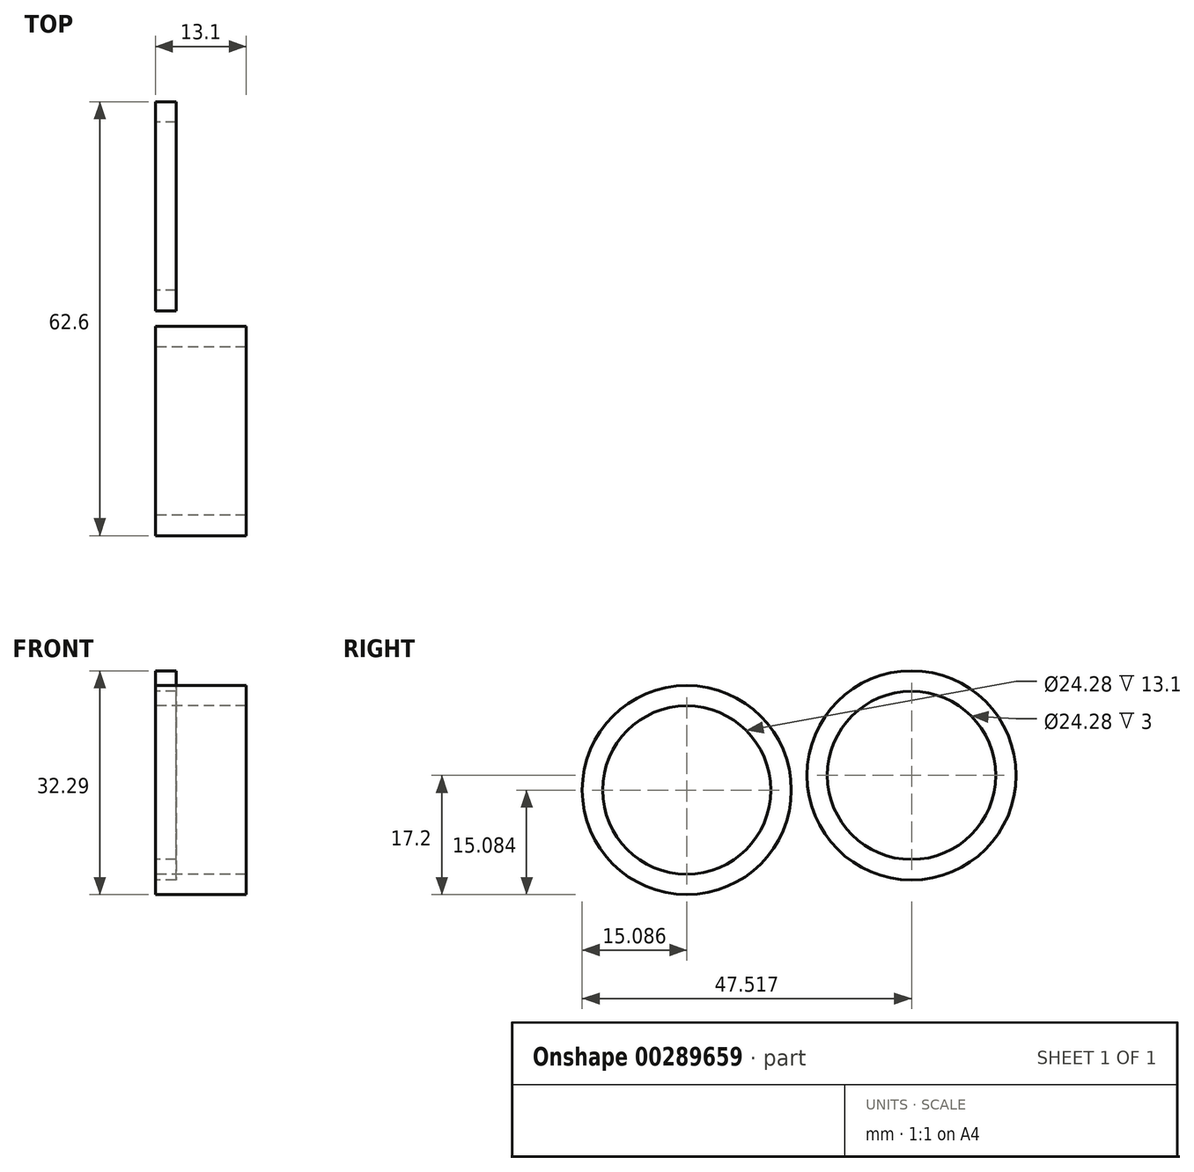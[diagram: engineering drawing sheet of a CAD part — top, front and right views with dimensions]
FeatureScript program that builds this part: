
annotation { "Feature Type Name" : "Feature", "Feature Type Description" : "" }
export const myFeature = defineFeature(function(context is Context, id is Id, definition is map)
    precondition{}
    {
        {
            var Q0;
            Q0=qCreatedBy(makeId("Right.planeOp"),FACE);
            var sketch = newSketch(context, id + "F0", { "sketchPlane" : qUnion([Q0])});
            skCircle(sketch, "E0", {"center": v(-30.12, 34.57) * mm, "radius": 15.09 * mm});
            skCircle(sketch, "E1", {"center": v(-30.12, 34.57) * mm, "radius": 12.14 * mm});
            skSolve(sketch);
        }
        {
            var Q0;
            Q0=makeQuery(id+"F0.imprint","IMPRINT",FACE,{"disambiguationData":[TD([[makeQuery(id+"F0.imprint","IMPRINT",EDGE,{"derivedFrom":sQuery(id+"F0.wireOp",EDGE,"E0")}),1.0]])]});
            extrude(context, id + "F1", {"entities" : qUnion([Q0]), "depth" : 3 * mm});
        }
        {
            var Q0;
            Q0=qCreatedBy(makeId("Right.planeOp"),FACE);
            var sketch = newSketch(context, id + "F2", { "sketchPlane" : qUnion([Q0])});
            skCircle(sketch, "E2", {"center": v(-62.55, 32.45) * mm, "radius": 15.09 * mm});
            skCircle(sketch, "E3", {"center": v(-62.55, 32.45) * mm, "radius": 12.14 * mm});
            skSolve(sketch);
        }
        {
            var Q0;
            Q0 = qSketchRegion(id + "F2", true);
            extrude(context, id + "F3", {"entities" : qUnion([Q0]), "depth" : 13.1 * mm});
        }
    });
